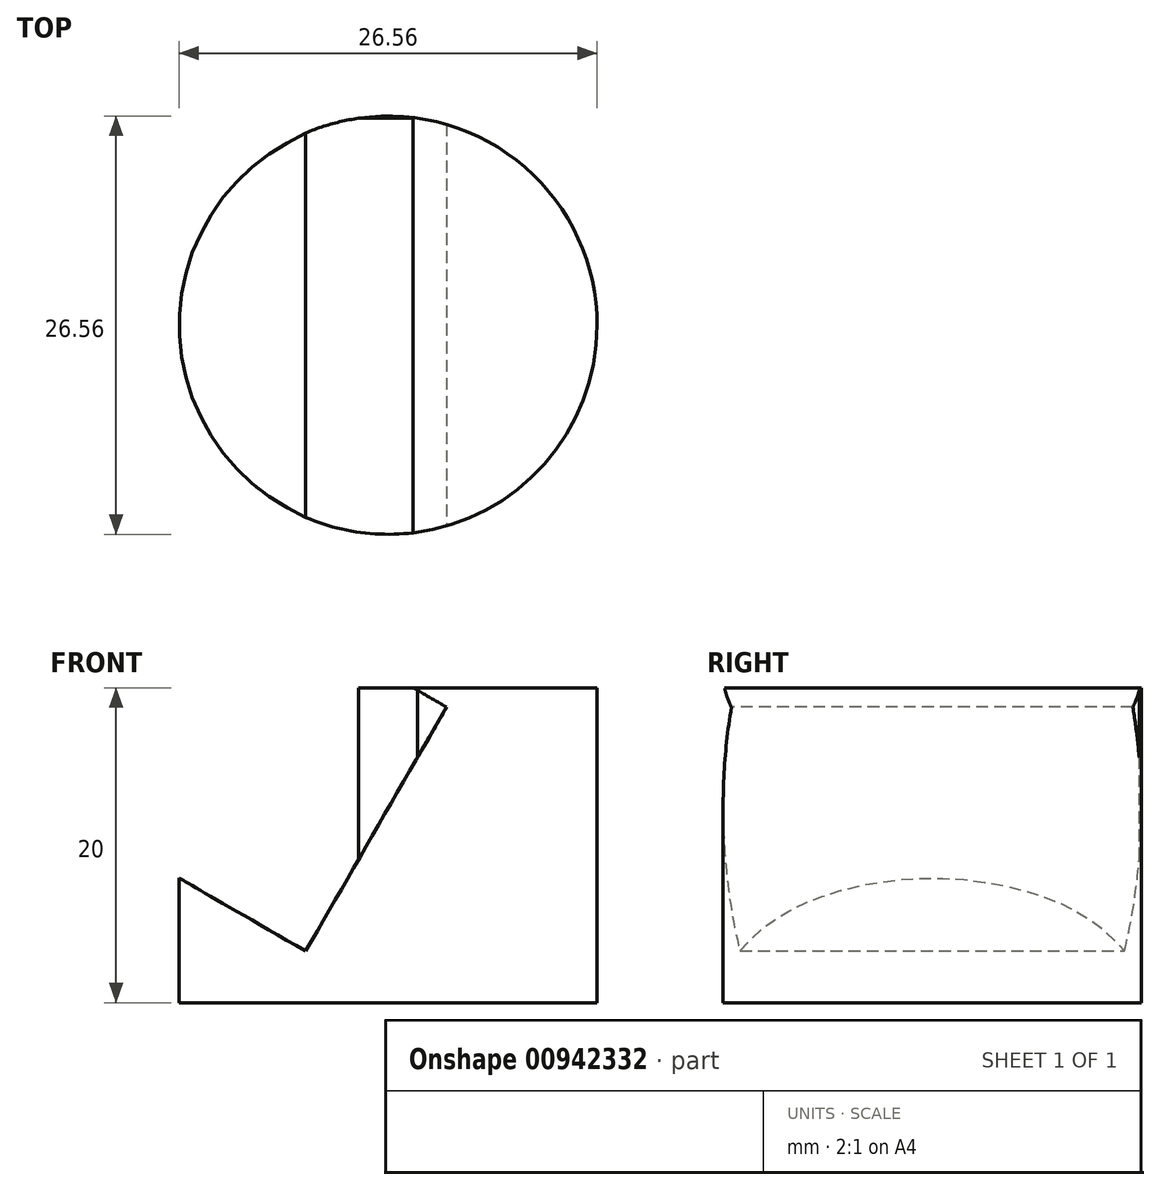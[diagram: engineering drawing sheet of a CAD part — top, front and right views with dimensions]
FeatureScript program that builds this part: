
annotation { "Feature Type Name" : "Feature", "Feature Type Description" : "" }
export const myFeature = defineFeature(function(context is Context, id is Id, definition is map)
    precondition{}
    {
        {
            var Q0;
            Q0=qCreatedBy(makeId("Front.planeOp"),FACE);
            var sketch = newSketch(context, id + "F0", { "sketchPlane" : qUnion([Q0])});
            skLineSegment(sketch, "E0.bottom", {"start": v(-13.28, 28.1) * mm, "end": v(13.28, 28.1) * mm});
            skLineSegment(sketch, "E0.top", {"start": v(-13.28, 8.1) * mm, "end": v(13.28, 8.1) * mm});
            skLineSegment(sketch, "E0.left", {"start": v(-13.28, 28.1) * mm, "end": v(-13.28, 8.1) * mm});
            skLineSegment(sketch, "E0.right", {"start": v(13.28, 28.1) * mm, "end": v(13.28, 8.1) * mm});
            skLineSegment(sketch, "E1.bottom", {"start": v(0, 28.1) * mm, "end": v(0, 28.1) * mm});
            skLineSegment(sketch, "E1.top", {"start": v(0, 8.1) * mm, "end": v(0, 8.1) * mm});
            skLineSegment(sketch, "E1.left", {"start": v(0, 28.1) * mm, "end": v(0, 8.1) * mm});
            skLineSegment(sketch, "E1.right", {"start": v(0, 28.1) * mm, "end": v(0, 8.1) * mm});
            skLineSegment(sketch, "E2", {"start": v(-13.28, 28.1) * mm, "end": v(13.28, 12.76) * mm});
            skSolve(sketch);
        }
        {
            var Q0;
            {var subQ0=sQuery(id+"F0.wireOp",EDGE,"E0.right");Q0=makeQuery(id+"F0.imprint","IMPRINT",FACE,{"disambiguationData":[TD([[makeQuery(id+"F0.imprint","IMPRINT",EDGE,{"derivedFrom":subQ0}),-1.0]])]});}
            var Q1;
            Q1=sQuery(id+"F0.wireOp",EDGE,"E1.right");
            revolve(context, id + "F1", {"surfaceOperationType" : NewSurfaceOperationType.NEW, "entities" : qUnion([Q0]), "axis" : qUnion([Q1]), "revolveType" : RevolveType.FULL});
        }
        {
            var Q0;
            Q0=sQuery(id+"F0.wireOp",EDGE,"E2");
            cPlane(context, id + "F2", {"entities" : qUnion([Q0]), "cplaneType" : CPlaneType.MID_PLANE, "offset" : 25 * mm, "width" : 150 * mm, "height" : 150 * mm});
        }
        {
            var Q0;
            Q0=qCreatedBy(id+"F2.planeOp",FACE);
            var sketch = newSketch(context, id + "F3", { "sketchPlane" : qUnion([Q0])});
            skLineSegment(sketch, "E3", {"start": v(-13.75, 7.23) * mm, "end": v(13.15, 7.23) * mm});
            skLineSegment(sketch, "E4", {"start": v(13.15, 7.23) * mm, "end": v(13.15, 25.12) * mm});
            skLineSegment(sketch, "E5", {"start": v(13.15, 25.12) * mm, "end": v(-13.75, 25.12) * mm});
            skLineSegment(sketch, "E6", {"start": v(-13.75, 25.12) * mm, "end": v(-13.75, 7.23) * mm});
            skSolve(sketch);
        }
        {
            var Q0;
            Q0=makeQuery(id+"F3.imprint","IMPRINT",FACE,{"disambiguationData":[TD([[makeQuery(id+"F3.imprint","IMPRINT",EDGE,{"derivedFrom":sQuery(id+"F3.wireOp",EDGE,"E3")}),1.0]])]});
            extrude(context, id + "F4", {"entities" : qUnion([Q0]), "operationType" : NewBodyOperationType.REMOVE, "oppositeDirection" : true, "depth" : 25 * mm, "offsetDistance" : 25 * mm});
        }
    });
